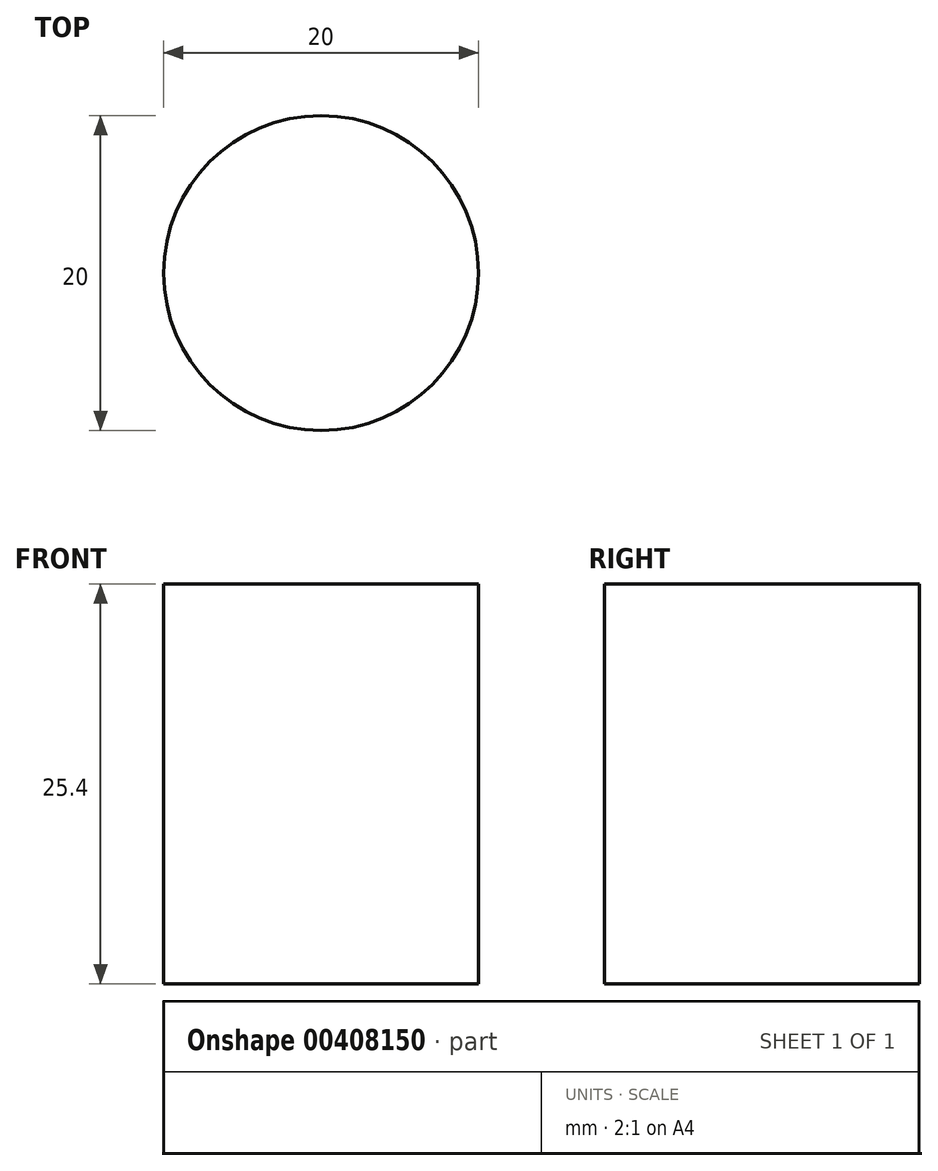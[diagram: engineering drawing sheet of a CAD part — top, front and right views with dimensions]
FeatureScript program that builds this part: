
annotation { "Feature Type Name" : "Feature", "Feature Type Description" : "" }
export const myFeature = defineFeature(function(context is Context, id is Id, definition is map)
    precondition{}
    {
        {
            var Q0;
            Q0=qCreatedBy(makeId("Top.planeOp"),FACE);
            var sketch = newSketch(context, id + "F0", { "sketchPlane" : qUnion([Q0])});
            skCircle(sketch, "E0", {"center": v(0, 0) * mm, "radius": 10 * mm});
            skSolve(sketch);
        }
        {
            var Q0;
            Q0=makeQuery(id+"F0.imprint","IMPRINT",FACE,{"disambiguationData":[TD([[makeQuery(id+"F0.imprint","IMPRINT",EDGE,{"derivedFrom":sQuery(id+"F0.wireOp",EDGE,"E0")}),1.0]])]});
            extrude(context, id + "F1", {"entities" : qUnion([Q0]), "depth" : 25.4 * mm});
        }
    });
